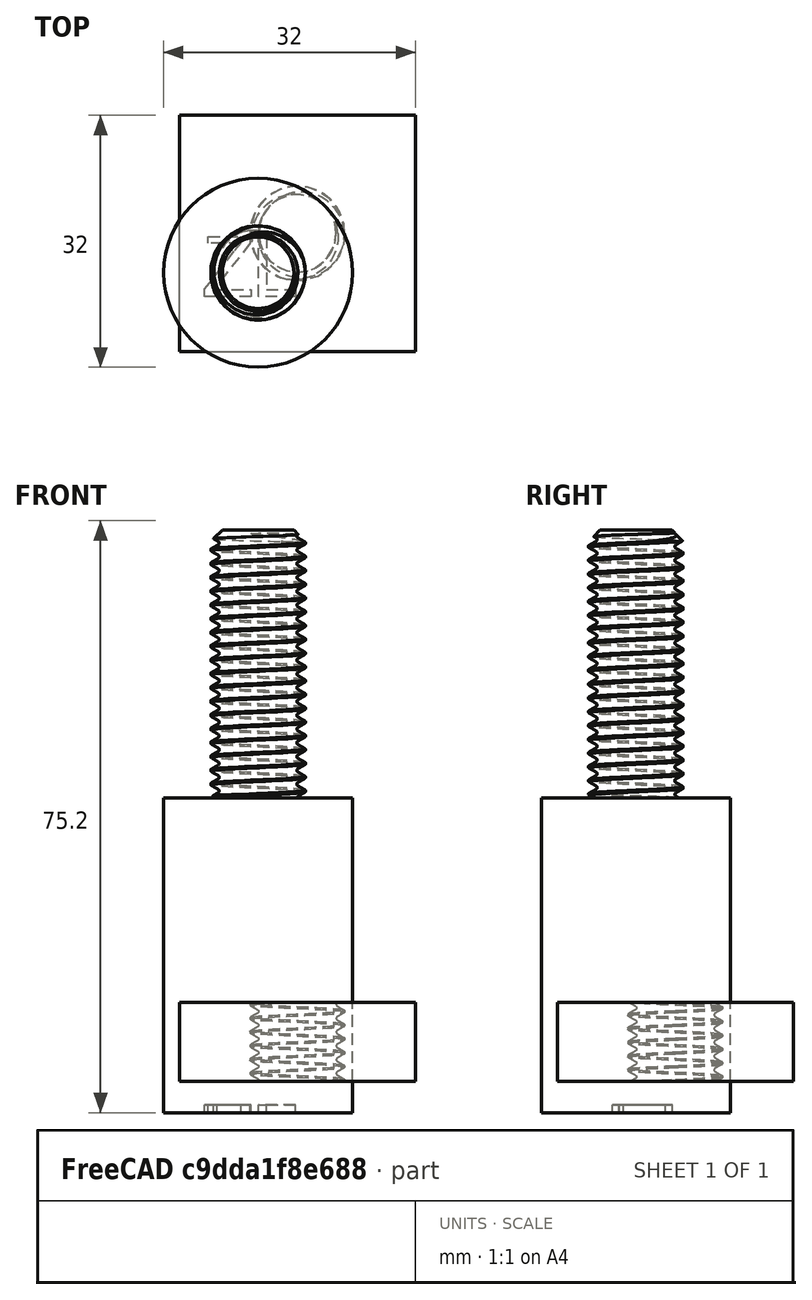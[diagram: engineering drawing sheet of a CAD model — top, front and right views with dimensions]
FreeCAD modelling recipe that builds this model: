
FCSTD DOCUMENT  (FreeCAD 0.19R24291 (Git))
Label: Na_kolesa_ukazovatel
License: All rights reserved
LicenseURL: http://en.wikipedia.org/wiki/All_rights_reserved
objects: Part::Cut×2, Part::FeaturePython×1, PartDesign::Body×1, Part::Part2DObjectPython×1, Part::Extrusion×1, Part::Cylinder×1, Part::MultiFuse×1, Part::Box×1, Part::Feature×1
note: 10 computed .brp shape members not serialized (recipe doc carries the construction recipe); baked Part::Feature solids carry a one-line shape summary decoded from their .brp

FEATURE [Part::FeaturePython] ThreadedRod  label="M12x35.0-ThreadedRod"  # Fasteners workbench fastener (typed FeaturePython)
  Placement = pos=(0,1.1e-15,74) rot=(0,0,1;0rad)
  diameter = 11
  invert = false
  length = 35
  matchOuter = false
  offset = 0
  thread = true
FEATURE [PartDesign::Body] Body
  Origin = -> Origin
FEATURE [Part::Part2DObjectPython] ShapeString  # Draft 2D object (typed FeaturePython)
  FontFile = <path>
  Placement = pos=(-7,-3,0) rot=(0,0,1;0rad)
  Size = 8
  String = ZL
  Tracking = 0
FEATURE [Part::Extrusion] Extrude
  Base = -> ShapeString
  Dir = (0,0,1)
  DirMode = 2
  FaceMakerClass = Part::FaceMakerBullseye
  LengthFwd = 1
  LengthRev = 0
  Solid = false
  Symmetric = false
FEATURE [Part::Cylinder] Cylinder
  Angle = 360
  AttacherType = Attacher::AttachEngine3D
  Height = 40
  Radius = 12
FEATURE [Part::MultiFuse] Fusion001  label="Fusionx"
  Shapes = -> [ThreadedRod,Cylinder]
FEATURE [Part::Cut] Cut  label="Srob_ukazovatel"
  Base = -> Fusion001
  Tool = -> Extrude
FEATURE [Part::Box] Box  label="Cube"
  AttacherType = Attacher::AttachEngine3D
  Height = 10
  Length = 30
  Placement = pos=(-10,-10,4) rot=(0,0,1;0rad)
  Width = 30
FEATURE [Part::Feature] ThreadedRod001  label="M12x40.0-ThreadedRod001"
  Placement = pos=(5,5,32) rot=(0,0,1;0rad)
  shape: bbox 15.65 x 17.56 x 42 mm, 95 faces (baked)
FEATURE [Part::Cut] Cut001  label="Matka"
  Base = -> Box
  Tool = -> ThreadedRod001
note: 1 file-system path scrubbed to <path> (originals preserved in the JSON sidecar)
